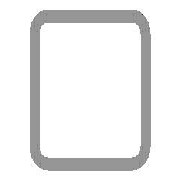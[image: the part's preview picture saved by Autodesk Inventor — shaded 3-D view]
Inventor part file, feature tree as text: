
AUTODESK INVENTOR PART (.ipt)
format: ipt  version: 2017 (Build 210142000, 142)  size: 131,584 bytes
history: native  units: mm (DEFAULTED — no unit token found)
features: other x3, sketch x3, plane x1
ambient origin geometry x8: Origin, YZ Plane, XZ Plane, XY Plane, X Axis, Y Axis, Z Axis, Center Point
bodies: Solid1 (feature_tree), Body (feature_tree)
feature tree (7):
  other  "Driven Length"
  other  "Start plane"
  other  "End plane"
  sketch  "Sketch"  dims[d7=2.25mm d10=40.0mm d11=40.0mm d12=1.5mm d13=-0.0mm d14=840.0mm d15=20.0mm d16=20.0mm d17=90.0deg d18=840.0mm]
  sketch  "Sketch3"  dims[d3=840.0mm]
  plane  "Work Plane3"
  sketch  "Sketch4"  dims[d4=0.0mm]
